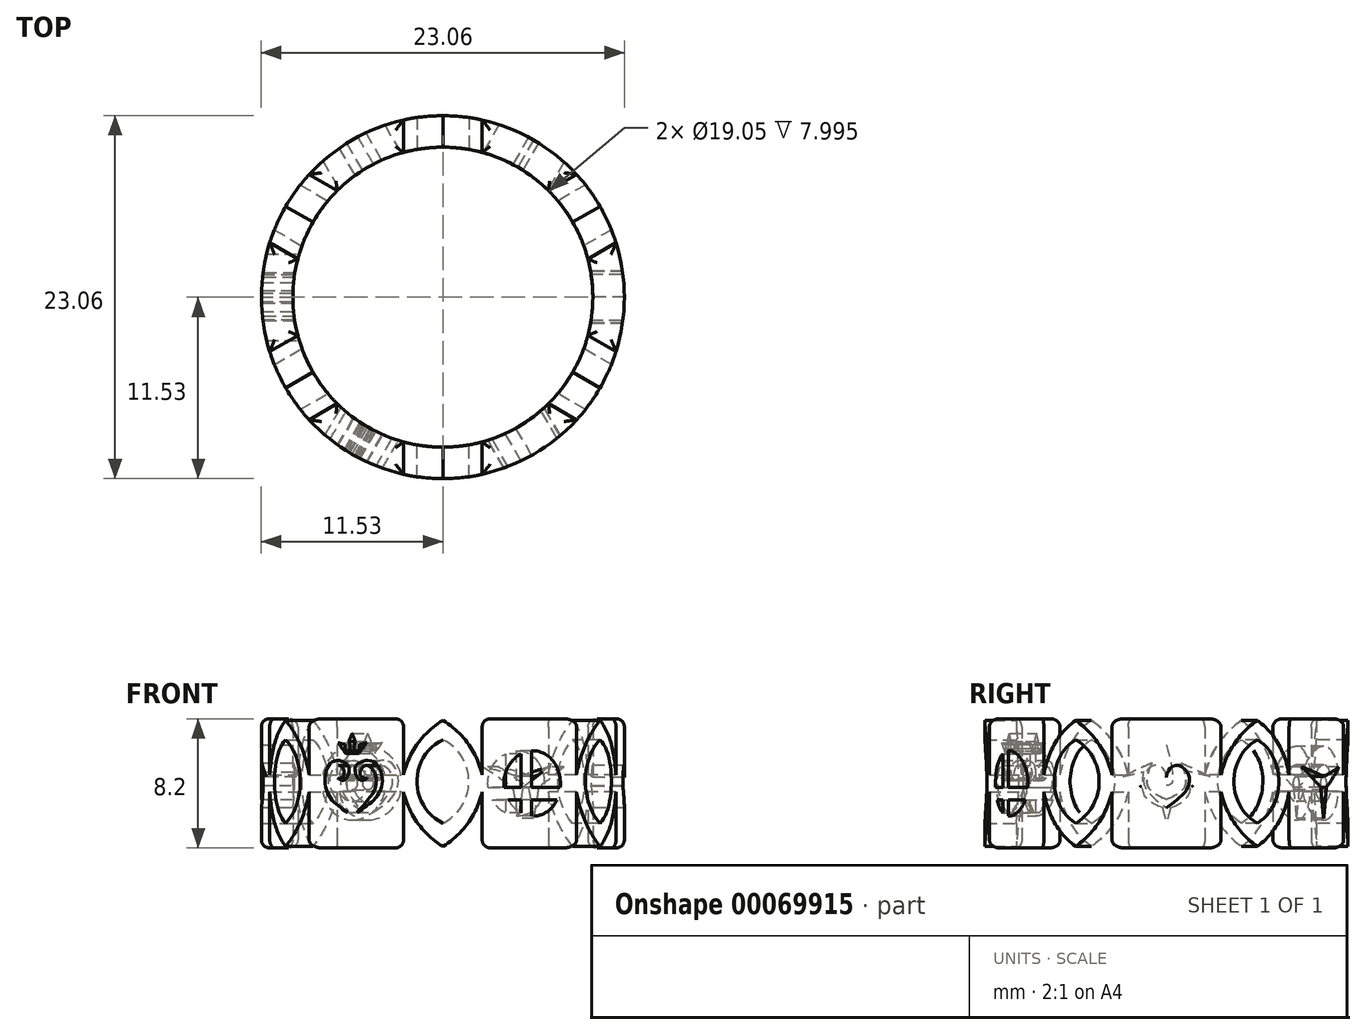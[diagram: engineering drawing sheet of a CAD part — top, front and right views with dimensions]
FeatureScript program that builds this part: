
annotation { "Feature Type Name" : "Feature", "Feature Type Description" : "" }
export const myFeature = defineFeature(function(context is Context, id is Id, definition is map)
    precondition{}
    {
        {
            var Q0;
            Q0=qCreatedBy(makeId("Front.planeOp"),FACE);
            var sketch = newSketch(context, id + "F0", { "sketchPlane" : qUnion([Q0])});
            skLineSegment(sketch, "E0", {"start": v(-9.53, 0) * mm, "end": v(9.53, 0) * mm, "construction": true});
            skLineSegment(sketch, "E1", {"start": v(9.53, -6.35) * mm, "end": v(9.53, 6.35) * mm, "construction": true});
            skLineSegment(sketch, "E2", {"start": v(9.53, -6.35) * mm, "end": v(9.53, 6.35) * mm});
            skLineSegment(sketch, "E3", {"start": v(9.53, -6.35) * mm, "end": v(11.53, -6.35) * mm});
            skLineSegment(sketch, "E4", {"start": v(11.53, 6.35) * mm, "end": v(11.53, -6.35) * mm});
            skLineSegment(sketch, "E5", {"start": v(0, 0) * mm, "end": v(0, 9.27) * mm, "construction": true});
            skLineSegment(sketch, "E6", {"start": v(9.53, 6.35) * mm, "end": v(11.53, 6.35) * mm});
            skSolve(sketch);
        }
        {
            var Q0;
            Q0=makeQuery(id+"F0.imprint","IMPRINT",FACE,{"disambiguationData":[TD([[makeQuery(id+"F0.imprint","IMPRINT",EDGE,{"derivedFrom":sQuery(id+"F0.wireOp",EDGE,"E2")}),-1.0]])]});
            var Q1;
            Q1=sQuery(id+"F0.wireOp",EDGE,"E5");
            revolve(context, id + "F1", {"entities" : qUnion([Q0]), "axis" : qUnion([Q1]), "revolveType" : RevolveType.FULL});
        }
        {
            var Q0;
            Q0=qCreatedBy(makeId("Front.planeOp"),FACE);
            var sketch = newSketch(context, id + "F2", { "sketchPlane" : qUnion([Q0])});
            skArc(sketch, "E7", {"start": v(0, -2.53) * mm, "mid": v(1.65, 0.12) * mm, "end": v(0, 2.77) * mm});
            skArc(sketch, "E8", {"start": v(0, 2.77) * mm, "mid": v(-1.65, 0.12) * mm, "end": v(0, -2.53) * mm});
            skSolve(sketch);
        }
        {
            var Q0;
            Q0=makeQuery(id+"F2.imprint","IMPRINT",FACE,{"disambiguationData":[TD([[makeQuery(id+"F2.imprint","IMPRINT",EDGE,{"derivedFrom":sQuery(id+"F2.wireOp",EDGE,"E7")}),1.0]])]});
            extrude(context, id + "F3", {"entities" : qUnion([Q0]), "operationType" : NewBodyOperationType.REMOVE, "oppositeDirection" : true, "depth" : 25 * mm});
        }
        {
            var Q0;
            Q0=makeQuery(id+"F3.boolean.opBoolean","COPY",FACE,{"derivedFrom":makeQuery(id+"F3.opExtrude","SWEPT_FACE",FACE,{"disambiguationData":[OSD([sQuery(id+"F2.wireOp",EDGE,"E8")])]})});
            var Q1;
            Q1=makeQuery(id+"F3.boolean.opBoolean","COPY",FACE,{"derivedFrom":makeQuery(id+"F3.opExtrude","SWEPT_FACE",FACE,{"disambiguationData":[OSD([sQuery(id+"F2.wireOp",EDGE,"E7")])]})});
            var Q2;
            Q2=makeQuery(id+"F1.opRevolve","SWEPT_FACE",FACE,{"disambiguationData":[OSD([sQuery(id+"F0.wireOp",EDGE,"E2")])]});
            circularPattern(context, id + "F4", {"faces" : qUnion([Q0, Q1]), "axis" : qUnion([Q2]), "angle" : 360 * degree, "instanceCount" : 6, "equalSpace" : true, "patternType" : PatternType.FACE});
        }
        {
            var Q0;
            Q0=qCreatedBy(makeId("Front.planeOp"),FACE);
            var sketch = newSketch(context, id + "F5", { "sketchPlane" : qUnion([Q0])});
            skArc(sketch, "E9", {"start": v(2.5, 0.53) * mm, "mid": v(1.6, 2.52) * mm, "end": v(0, 4) * mm});
            skArc(sketch, "E10.MirrorCS", {"start": v(-2.5, 0.53) * mm, "mid": v(-1.6, 2.52) * mm, "end": v(0, 4) * mm});
            skLineSegment(sketch, "E11", {"start": v(-2.5, 0.53) * mm, "end": v(-2.5, 6.68) * mm});
            skLineSegment(sketch, "E12", {"start": v(-2.5, 6.68) * mm, "end": v(2.5, 6.68) * mm});
            skLineSegment(sketch, "E13", {"start": v(2.5, 6.68) * mm, "end": v(2.5, 0.53) * mm});
            skArc(sketch, "E14.MirrorCS", {"start": v(-2.5, -0.53) * mm, "mid": v(-1.6, -2.52) * mm, "end": v(0, -4) * mm});
            skArc(sketch, "E15.MirrorCS", {"start": v(2.5, -0.53) * mm, "mid": v(1.6, -2.52) * mm, "end": v(0, -4) * mm});
            skLineSegment(sketch, "E16.MirrorCS", {"start": v(2.5, -6.68) * mm, "end": v(2.5, -0.53) * mm});
            skLineSegment(sketch, "E17.MirrorCS", {"start": v(-2.5, -0.53) * mm, "end": v(-2.5, -6.68) * mm});
            skLineSegment(sketch, "E18.MirrorCS", {"start": v(-2.5, -6.68) * mm, "end": v(2.5, -6.68) * mm});
            skSolve(sketch);
        }
        {
            var Q0;
            Q0=makeQuery(id+"F5.imprint","IMPRINT",FACE,{"disambiguationData":[TD([[makeQuery(id+"F5.imprint","IMPRINT",EDGE,{"derivedFrom":sQuery(id+"F5.wireOp",EDGE,"E9")}),-1.0]])]});
            extrude(context, id + "F6", {"entities" : qUnion([Q0]), "operationType" : NewBodyOperationType.REMOVE, "oppositeDirection" : true, "depth" : 25 * mm});
        }
        {
            var Q0;
            Q0=makeQuery(id+"F6.boolean.opBoolean","COPY",FACE,{"derivedFrom":makeQuery(id+"F6.opExtrude","SWEPT_FACE",FACE,{"disambiguationData":[OSD([sQuery(id+"F5.wireOp",EDGE,"E10.MirrorCS")])]})});
            var Q1;
            Q1=makeQuery(id+"F6.boolean.opBoolean","COPY",FACE,{"derivedFrom":makeQuery(id+"F6.opExtrude","SWEPT_FACE",FACE,{"disambiguationData":[OSD([sQuery(id+"F5.wireOp",EDGE,"E9")])]})});
            var Q2;
            Q2=makeQuery(id+"F6.boolean.opBoolean","COPY",FACE,{"derivedFrom":makeQuery(id+"F6.opExtrude","SWEPT_FACE",FACE,{"disambiguationData":[OSD([sQuery(id+"F5.wireOp",EDGE,"E11")])]})});
            var Q3;
            Q3=makeQuery(id+"F6.boolean.opBoolean","COPY",FACE,{"derivedFrom":makeQuery(id+"F6.opExtrude","SWEPT_FACE",FACE,{"disambiguationData":[OSD([sQuery(id+"F5.wireOp",EDGE,"E13")])]})});
            var Q4;
            Q4=makeQuery(id+"F1.opRevolve","SWEPT_FACE",FACE,{"disambiguationData":[OSD([sQuery(id+"F0.wireOp",EDGE,"E4")])]});
            circularPattern(context, id + "F7", {"faces" : qUnion([Q0, Q1, Q2, Q3]), "axis" : qUnion([Q4]), "angle" : 360 * degree, "instanceCount" : 12, "equalSpace" : true, "patternType" : PatternType.FACE});
        }
        {
            var Q0;
            Q0=makeQuery(id+"F1.opRevolve","SWEPT_EDGE",EDGE,{"disambiguationData":[OSD([sQuery(id+"F0.wireOp",EDGE,"E3"),sQuery(id+"F0.wireOp",EDGE,"E4")])]});
            cPlane(context, id + "F8", {"entities" : qUnion([Q0]), "cplaneType" : CPlaneType.LINE_ANGLE, "offset" : 150 * mm, "angle" : 0 * degree, "width" : 150 * mm, "height" : 150 * mm});
        }
        {
            var Q0;
            Q0=makeQuery(id+"F5.imprint","IMPRINT",FACE,{"disambiguationData":[TD([[makeQuery(id+"F5.imprint","IMPRINT",EDGE,{"derivedFrom":sQuery(id+"F5.wireOp",EDGE,"E14.MirrorCS")}),-1.0]])]});
            extrude(context, id + "F9", {"entities" : qUnion([Q0]), "operationType" : NewBodyOperationType.REMOVE, "oppositeDirection" : true, "depth" : 25 * mm});
        }
        {
            var Q0;
            Q0=makeQuery(id+"F9.boolean.opBoolean","COPY",FACE,{"derivedFrom":makeQuery(id+"F9.opExtrude","SWEPT_FACE",FACE,{"disambiguationData":[OSD([sQuery(id+"F5.wireOp",EDGE,"E16.MirrorCS")])]})});
            var Q1;
            Q1=makeQuery(id+"F9.boolean.opBoolean","COPY",FACE,{"derivedFrom":makeQuery(id+"F9.opExtrude","SWEPT_FACE",FACE,{"disambiguationData":[OSD([sQuery(id+"F5.wireOp",EDGE,"E14.MirrorCS")])]})});
            var Q2;
            Q2=makeQuery(id+"F9.boolean.opBoolean","COPY",FACE,{"derivedFrom":makeQuery(id+"F9.opExtrude","SWEPT_FACE",FACE,{"disambiguationData":[OSD([sQuery(id+"F5.wireOp",EDGE,"E15.MirrorCS")])]})});
            var Q3;
            Q3=makeQuery(id+"F9.boolean.opBoolean","COPY",FACE,{"derivedFrom":makeQuery(id+"F9.opExtrude","SWEPT_FACE",FACE,{"disambiguationData":[OSD([sQuery(id+"F5.wireOp",EDGE,"E17.MirrorCS")])]})});
            var Q4;
            Q4=makeQuery(id+"F1.opRevolve","SWEPT_FACE",FACE,{"disambiguationData":[OSD([sQuery(id+"F0.wireOp",EDGE,"E4")])]});
            circularPattern(context, id + "F10", {"faces" : qUnion([Q0, Q1, Q2, Q3]), "axis" : qUnion([Q4]), "angle" : 360 * degree, "instanceCount" : 12, "oppositeDirection" : true, "equalSpace" : true, "patternType" : PatternType.FACE});
        }
        {
            var Q0;
            Q0=qCreatedBy(makeId("Front.planeOp"),FACE);
            var sketch = newSketch(context, id + "F11", { "sketchPlane" : qUnion([Q0])});
            skLineSegment(sketch, "E19.bottom", {"start": v(-11.85, 7.08) * mm, "end": v(-8.83, 7.08) * mm});
            skLineSegment(sketch, "E19.top", {"start": v(-11.85, 4.1) * mm, "end": v(-8.83, 4.1) * mm});
            skLineSegment(sketch, "E19.left", {"start": v(-11.85, 7.08) * mm, "end": v(-11.85, 4.1) * mm});
            skLineSegment(sketch, "E19.right", {"start": v(-8.83, 7.08) * mm, "end": v(-8.83, 4.1) * mm});
            skLineSegment(sketch, "E20.MirrorCS", {"start": v(-11.85, -7.08) * mm, "end": v(-11.85, -4.1) * mm});
            skLineSegment(sketch, "E21.MirrorCS", {"start": v(-11.85, -4.1) * mm, "end": v(-8.83, -4.1) * mm});
            skLineSegment(sketch, "E22.MirrorCS", {"start": v(-8.83, -7.08) * mm, "end": v(-8.83, -4.1) * mm});
            skLineSegment(sketch, "E23.MirrorCS", {"start": v(-11.85, -7.08) * mm, "end": v(-8.83, -7.08) * mm});
            skSolve(sketch);
        }
        {
            var Q0;
            Q0=makeQuery(id+"F11.imprint","IMPRINT",FACE,{"disambiguationData":[TD([[makeQuery(id+"F11.imprint","IMPRINT",EDGE,{"derivedFrom":sQuery(id+"F11.wireOp",EDGE,"E19.bottom")}),-1.0]])]});
            var Q1;
            Q1=sQuery(id+"F0.wireOp",EDGE,"E5");
            revolve(context, id + "F12", {"operationType" : NewBodyOperationType.REMOVE, "entities" : qUnion([Q0]), "axis" : qUnion([Q1]), "revolveType" : RevolveType.FULL, "oppositeDirection" : true});
        }
        {
            var Q0;
            Q0=makeQuery(id+"F11.imprint","IMPRINT",FACE,{"disambiguationData":[TD([[makeQuery(id+"F11.imprint","IMPRINT",EDGE,{"derivedFrom":sQuery(id+"F11.wireOp",EDGE,"E20.MirrorCS")}),-1.0]])]});
            var Q1;
            Q1=sQuery(id+"F0.wireOp",EDGE,"E5");
            revolve(context, id + "F13", {"operationType" : NewBodyOperationType.REMOVE, "entities" : qUnion([Q0]), "axis" : qUnion([Q1]), "revolveType" : RevolveType.FULL, "oppositeDirection" : true});
        }
        {
            var Q0;
            Q0=makeQuery(id+"F13.boolean.opBoolean","INTERSECT",EDGE,{"disambiguationData":[OD(3.0)],"derivedFrom":[makeQuery(id+"F1.opRevolve","SWEPT_FACE",FACE,{"disambiguationData":[OSD([sQuery(id+"F0.wireOp",EDGE,"E2")])]}),makeQuery(id+"F13.opRevolve","SWEPT_FACE",FACE,{"disambiguationData":[OSD([sQuery(id+"F11.wireOp",EDGE,"E21.MirrorCS")])]})]});
            var Q1;
            Q1=makeQuery(id+"F13.boolean.opBoolean","INTERSECT",EDGE,{"disambiguationData":[OD(4.0)],"derivedFrom":[makeQuery(id+"F1.opRevolve","SWEPT_FACE",FACE,{"disambiguationData":[OSD([sQuery(id+"F0.wireOp",EDGE,"E2")])]}),makeQuery(id+"F13.opRevolve","SWEPT_FACE",FACE,{"disambiguationData":[OSD([sQuery(id+"F11.wireOp",EDGE,"E21.MirrorCS")])]})]});
            var Q2;
            Q2=makeQuery(id+"F13.boolean.opBoolean","INTERSECT",EDGE,{"disambiguationData":[OD(5.0)],"derivedFrom":[makeQuery(id+"F1.opRevolve","SWEPT_FACE",FACE,{"disambiguationData":[OSD([sQuery(id+"F0.wireOp",EDGE,"E2")])]}),makeQuery(id+"F13.opRevolve","SWEPT_FACE",FACE,{"disambiguationData":[OSD([sQuery(id+"F11.wireOp",EDGE,"E21.MirrorCS")])]})]});
            var Q3;
            Q3=makeQuery(id+"F13.boolean.opBoolean","INTERSECT",EDGE,{"disambiguationData":[OD(0.0)],"derivedFrom":[makeQuery(id+"F1.opRevolve","SWEPT_FACE",FACE,{"disambiguationData":[OSD([sQuery(id+"F0.wireOp",EDGE,"E2")])]}),makeQuery(id+"F13.opRevolve","SWEPT_FACE",FACE,{"disambiguationData":[OSD([sQuery(id+"F11.wireOp",EDGE,"E21.MirrorCS")])]})]});
            var Q4;
            Q4=makeQuery(id+"F13.boolean.opBoolean","INTERSECT",EDGE,{"disambiguationData":[OD(1.0)],"derivedFrom":[makeQuery(id+"F1.opRevolve","SWEPT_FACE",FACE,{"disambiguationData":[OSD([sQuery(id+"F0.wireOp",EDGE,"E2")])]}),makeQuery(id+"F13.opRevolve","SWEPT_FACE",FACE,{"disambiguationData":[OSD([sQuery(id+"F11.wireOp",EDGE,"E21.MirrorCS")])]})]});
            var Q5;
            Q5=makeQuery(id+"F13.boolean.opBoolean","INTERSECT",EDGE,{"disambiguationData":[OD(2.0)],"derivedFrom":[makeQuery(id+"F1.opRevolve","SWEPT_FACE",FACE,{"disambiguationData":[OSD([sQuery(id+"F0.wireOp",EDGE,"E2")])]}),makeQuery(id+"F13.opRevolve","SWEPT_FACE",FACE,{"disambiguationData":[OSD([sQuery(id+"F11.wireOp",EDGE,"E21.MirrorCS")])]})]});
            var Q6;
            Q6=makeQuery(id+"F12.boolean.opBoolean","INTERSECT",EDGE,{"disambiguationData":[OD(4.0)],"derivedFrom":[makeQuery(id+"F1.opRevolve","SWEPT_FACE",FACE,{"disambiguationData":[OSD([sQuery(id+"F0.wireOp",EDGE,"E2")])]}),makeQuery(id+"F12.opRevolve","SWEPT_FACE",FACE,{"disambiguationData":[OSD([sQuery(id+"F11.wireOp",EDGE,"E19.top")])]})]});
            var Q7;
            Q7=makeQuery(id+"F12.boolean.opBoolean","INTERSECT",EDGE,{"disambiguationData":[OD(3.0)],"derivedFrom":[makeQuery(id+"F1.opRevolve","SWEPT_FACE",FACE,{"disambiguationData":[OSD([sQuery(id+"F0.wireOp",EDGE,"E2")])]}),makeQuery(id+"F12.opRevolve","SWEPT_FACE",FACE,{"disambiguationData":[OSD([sQuery(id+"F11.wireOp",EDGE,"E19.top")])]})]});
            var Q8;
            Q8=makeQuery(id+"F12.boolean.opBoolean","INTERSECT",EDGE,{"disambiguationData":[OD(2.0)],"derivedFrom":[makeQuery(id+"F1.opRevolve","SWEPT_FACE",FACE,{"disambiguationData":[OSD([sQuery(id+"F0.wireOp",EDGE,"E2")])]}),makeQuery(id+"F12.opRevolve","SWEPT_FACE",FACE,{"disambiguationData":[OSD([sQuery(id+"F11.wireOp",EDGE,"E19.top")])]})]});
            var Q9;
            Q9=makeQuery(id+"F12.boolean.opBoolean","INTERSECT",EDGE,{"disambiguationData":[OD(1.0)],"derivedFrom":[makeQuery(id+"F1.opRevolve","SWEPT_FACE",FACE,{"disambiguationData":[OSD([sQuery(id+"F0.wireOp",EDGE,"E2")])]}),makeQuery(id+"F12.opRevolve","SWEPT_FACE",FACE,{"disambiguationData":[OSD([sQuery(id+"F11.wireOp",EDGE,"E19.top")])]})]});
            var Q10;
            Q10=makeQuery(id+"F12.boolean.opBoolean","INTERSECT",EDGE,{"disambiguationData":[OD(0.0)],"derivedFrom":[makeQuery(id+"F1.opRevolve","SWEPT_FACE",FACE,{"disambiguationData":[OSD([sQuery(id+"F0.wireOp",EDGE,"E2")])]}),makeQuery(id+"F12.opRevolve","SWEPT_FACE",FACE,{"disambiguationData":[OSD([sQuery(id+"F11.wireOp",EDGE,"E19.top")])]})]});
            var Q11;
            Q11=makeQuery(id+"F12.boolean.opBoolean","INTERSECT",EDGE,{"disambiguationData":[OD(5.0)],"derivedFrom":[makeQuery(id+"F1.opRevolve","SWEPT_FACE",FACE,{"disambiguationData":[OSD([sQuery(id+"F0.wireOp",EDGE,"E2")])]}),makeQuery(id+"F12.opRevolve","SWEPT_FACE",FACE,{"disambiguationData":[OSD([sQuery(id+"F11.wireOp",EDGE,"E19.top")])]})]});
            fillet(context, id + "F14", {"entities" : qUnion([Q0, Q1, Q2, Q3, Q4, Q5, Q6, Q7, Q8, Q9, Q10, Q11]), "radius" : .5 * mm, "tangentPropagation" : true, "allowEdgeOverflow" : false});
        }
        {
            var Q0;
            Q0=makeQuery(id+"F12.boolean.opBoolean","INTERSECT",EDGE,{"disambiguationData":[OD(2.0)],"derivedFrom":[makeQuery(id+"F1.opRevolve","SWEPT_FACE",FACE,{"disambiguationData":[OSD([sQuery(id+"F0.wireOp",EDGE,"E4")])]}),makeQuery(id+"F12.opRevolve","SWEPT_FACE",FACE,{"disambiguationData":[OSD([sQuery(id+"F11.wireOp",EDGE,"E19.top")])]})]});
            var Q1;
            Q1=makeQuery(id+"F13.boolean.opBoolean","INTERSECT",EDGE,{"disambiguationData":[OD(5.0)],"derivedFrom":[makeQuery(id+"F1.opRevolve","SWEPT_FACE",FACE,{"disambiguationData":[OSD([sQuery(id+"F0.wireOp",EDGE,"E4")])]}),makeQuery(id+"F13.opRevolve","SWEPT_FACE",FACE,{"disambiguationData":[OSD([sQuery(id+"F11.wireOp",EDGE,"E21.MirrorCS")])]})]});
            var Q2;
            Q2=makeQuery(id+"F13.boolean.opBoolean","INTERSECT",EDGE,{"disambiguationData":[OD(4.0)],"derivedFrom":[makeQuery(id+"F1.opRevolve","SWEPT_FACE",FACE,{"disambiguationData":[OSD([sQuery(id+"F0.wireOp",EDGE,"E4")])]}),makeQuery(id+"F13.opRevolve","SWEPT_FACE",FACE,{"disambiguationData":[OSD([sQuery(id+"F11.wireOp",EDGE,"E21.MirrorCS")])]})]});
            var Q3;
            Q3=makeQuery(id+"F12.boolean.opBoolean","INTERSECT",EDGE,{"disambiguationData":[OD(3.0)],"derivedFrom":[makeQuery(id+"F1.opRevolve","SWEPT_FACE",FACE,{"disambiguationData":[OSD([sQuery(id+"F0.wireOp",EDGE,"E4")])]}),makeQuery(id+"F12.opRevolve","SWEPT_FACE",FACE,{"disambiguationData":[OSD([sQuery(id+"F11.wireOp",EDGE,"E19.top")])]})]});
            var Q4;
            Q4=makeQuery(id+"F13.boolean.opBoolean","INTERSECT",EDGE,{"disambiguationData":[OD(3.0)],"derivedFrom":[makeQuery(id+"F1.opRevolve","SWEPT_FACE",FACE,{"disambiguationData":[OSD([sQuery(id+"F0.wireOp",EDGE,"E4")])]}),makeQuery(id+"F13.opRevolve","SWEPT_FACE",FACE,{"disambiguationData":[OSD([sQuery(id+"F11.wireOp",EDGE,"E21.MirrorCS")])]})]});
            var Q5;
            Q5=makeQuery(id+"F12.boolean.opBoolean","INTERSECT",EDGE,{"disambiguationData":[OD(4.0)],"derivedFrom":[makeQuery(id+"F1.opRevolve","SWEPT_FACE",FACE,{"disambiguationData":[OSD([sQuery(id+"F0.wireOp",EDGE,"E4")])]}),makeQuery(id+"F12.opRevolve","SWEPT_FACE",FACE,{"disambiguationData":[OSD([sQuery(id+"F11.wireOp",EDGE,"E19.top")])]})]});
            var Q6;
            Q6=makeQuery(id+"F12.boolean.opBoolean","INTERSECT",EDGE,{"disambiguationData":[OD(5.0)],"derivedFrom":[makeQuery(id+"F1.opRevolve","SWEPT_FACE",FACE,{"disambiguationData":[OSD([sQuery(id+"F0.wireOp",EDGE,"E4")])]}),makeQuery(id+"F12.opRevolve","SWEPT_FACE",FACE,{"disambiguationData":[OSD([sQuery(id+"F11.wireOp",EDGE,"E19.top")])]})]});
            var Q7;
            Q7=makeQuery(id+"F13.boolean.opBoolean","INTERSECT",EDGE,{"disambiguationData":[OD(2.0)],"derivedFrom":[makeQuery(id+"F1.opRevolve","SWEPT_FACE",FACE,{"disambiguationData":[OSD([sQuery(id+"F0.wireOp",EDGE,"E4")])]}),makeQuery(id+"F13.opRevolve","SWEPT_FACE",FACE,{"disambiguationData":[OSD([sQuery(id+"F11.wireOp",EDGE,"E21.MirrorCS")])]})]});
            var Q8;
            Q8=makeQuery(id+"F12.boolean.opBoolean","INTERSECT",EDGE,{"disambiguationData":[OD(0.0)],"derivedFrom":[makeQuery(id+"F1.opRevolve","SWEPT_FACE",FACE,{"disambiguationData":[OSD([sQuery(id+"F0.wireOp",EDGE,"E4")])]}),makeQuery(id+"F12.opRevolve","SWEPT_FACE",FACE,{"disambiguationData":[OSD([sQuery(id+"F11.wireOp",EDGE,"E19.top")])]})]});
            var Q9;
            Q9=makeQuery(id+"F13.boolean.opBoolean","INTERSECT",EDGE,{"disambiguationData":[OD(1.0)],"derivedFrom":[makeQuery(id+"F1.opRevolve","SWEPT_FACE",FACE,{"disambiguationData":[OSD([sQuery(id+"F0.wireOp",EDGE,"E4")])]}),makeQuery(id+"F13.opRevolve","SWEPT_FACE",FACE,{"disambiguationData":[OSD([sQuery(id+"F11.wireOp",EDGE,"E21.MirrorCS")])]})]});
            var Q10;
            Q10=makeQuery(id+"F13.boolean.opBoolean","INTERSECT",EDGE,{"disambiguationData":[OD(0.0)],"derivedFrom":[makeQuery(id+"F1.opRevolve","SWEPT_FACE",FACE,{"disambiguationData":[OSD([sQuery(id+"F0.wireOp",EDGE,"E4")])]}),makeQuery(id+"F13.opRevolve","SWEPT_FACE",FACE,{"disambiguationData":[OSD([sQuery(id+"F11.wireOp",EDGE,"E21.MirrorCS")])]})]});
            var Q11;
            Q11=makeQuery(id+"F12.boolean.opBoolean","INTERSECT",EDGE,{"disambiguationData":[OD(1.0)],"derivedFrom":[makeQuery(id+"F1.opRevolve","SWEPT_FACE",FACE,{"disambiguationData":[OSD([sQuery(id+"F0.wireOp",EDGE,"E4")])]}),makeQuery(id+"F12.opRevolve","SWEPT_FACE",FACE,{"disambiguationData":[OSD([sQuery(id+"F11.wireOp",EDGE,"E19.top")])]})]});
            fillet(context, id + "F15", {"entities" : qUnion([Q0, Q1, Q2, Q3, Q4, Q5, Q6, Q7, Q8, Q9, Q10, Q11]), "radius" : .5 * mm, "tangentPropagation" : true, "allowEdgeOverflow" : false});
        }
        {
            var Q0;
            Q0=makeQuery(id+"F12.boolean.opBoolean","INTERSECT",EDGE,{"derivedFrom":[makeQuery(id+"F7.opPattern","COPY",FACE,{"derivedFrom":makeQuery(id+"F6.boolean.opBoolean","COPY",FACE,{"derivedFrom":makeQuery(id+"F6.opExtrude","SWEPT_FACE",FACE,{"disambiguationData":[OSD([sQuery(id+"F5.wireOp",EDGE,"E11")])]})}),"instanceName":"6"}),makeQuery(id+"F12.opRevolve","SWEPT_FACE",FACE,{"disambiguationData":[OSD([sQuery(id+"F11.wireOp",EDGE,"E19.top")])]})]});
            var Q1;
            Q1=makeQuery(id+"F12.boolean.opBoolean","INTERSECT",EDGE,{"derivedFrom":[makeQuery(id+"F7.opPattern","COPY",FACE,{"derivedFrom":makeQuery(id+"F6.boolean.opBoolean","COPY",FACE,{"derivedFrom":makeQuery(id+"F6.opExtrude","SWEPT_FACE",FACE,{"disambiguationData":[OSD([sQuery(id+"F5.wireOp",EDGE,"E11")])]})}),"instanceName":"4"}),makeQuery(id+"F12.opRevolve","SWEPT_FACE",FACE,{"disambiguationData":[OSD([sQuery(id+"F11.wireOp",EDGE,"E19.top")])]})]});
            var Q2;
            Q2=makeQuery(id+"F12.boolean.opBoolean","INTERSECT",EDGE,{"derivedFrom":[makeQuery(id+"F7.opPattern","COPY",FACE,{"derivedFrom":makeQuery(id+"F6.boolean.opBoolean","COPY",FACE,{"derivedFrom":makeQuery(id+"F6.opExtrude","SWEPT_FACE",FACE,{"disambiguationData":[OSD([sQuery(id+"F5.wireOp",EDGE,"E13")])]})}),"instanceName":"4"}),makeQuery(id+"F12.opRevolve","SWEPT_FACE",FACE,{"disambiguationData":[OSD([sQuery(id+"F11.wireOp",EDGE,"E19.top")])]})]});
            var Q3;
            Q3=makeQuery(id+"F12.boolean.opBoolean","INTERSECT",EDGE,{"derivedFrom":[makeQuery(id+"F7.opPattern","COPY",FACE,{"derivedFrom":makeQuery(id+"F6.boolean.opBoolean","COPY",FACE,{"derivedFrom":makeQuery(id+"F6.opExtrude","SWEPT_FACE",FACE,{"disambiguationData":[OSD([sQuery(id+"F5.wireOp",EDGE,"E13")])]})}),"instanceName":"2"}),makeQuery(id+"F12.opRevolve","SWEPT_FACE",FACE,{"disambiguationData":[OSD([sQuery(id+"F11.wireOp",EDGE,"E19.top")])]})]});
            var Q4;
            Q4=makeQuery(id+"F12.boolean.opBoolean","INTERSECT",EDGE,{"derivedFrom":[makeQuery(id+"F7.opPattern","COPY",FACE,{"derivedFrom":makeQuery(id+"F6.boolean.opBoolean","COPY",FACE,{"derivedFrom":makeQuery(id+"F6.opExtrude","SWEPT_FACE",FACE,{"disambiguationData":[OSD([sQuery(id+"F5.wireOp",EDGE,"E11")])]})}),"instanceName":"2"}),makeQuery(id+"F12.opRevolve","SWEPT_FACE",FACE,{"disambiguationData":[OSD([sQuery(id+"F11.wireOp",EDGE,"E19.top")])]})]});
            var Q5;
            Q5=makeQuery(id+"F12.boolean.opBoolean","INTERSECT",EDGE,{"derivedFrom":[makeQuery(id+"F6.boolean.opBoolean","COPY",FACE,{"derivedFrom":makeQuery(id+"F6.opExtrude","SWEPT_FACE",FACE,{"disambiguationData":[OSD([sQuery(id+"F5.wireOp",EDGE,"E13")])]})}),makeQuery(id+"F12.opRevolve","SWEPT_FACE",FACE,{"disambiguationData":[OSD([sQuery(id+"F11.wireOp",EDGE,"E19.top")])]})]});
            var Q6;
            Q6=makeQuery(id+"F12.boolean.opBoolean","INTERSECT",EDGE,{"derivedFrom":[makeQuery(id+"F6.boolean.opBoolean","COPY",FACE,{"derivedFrom":makeQuery(id+"F6.opExtrude","SWEPT_FACE",FACE,{"disambiguationData":[OSD([sQuery(id+"F5.wireOp",EDGE,"E11")])]})}),makeQuery(id+"F12.opRevolve","SWEPT_FACE",FACE,{"disambiguationData":[OSD([sQuery(id+"F11.wireOp",EDGE,"E19.top")])]})]});
            var Q7;
            Q7=makeQuery(id+"F12.boolean.opBoolean","INTERSECT",EDGE,{"derivedFrom":[makeQuery(id+"F7.opPattern","COPY",FACE,{"derivedFrom":makeQuery(id+"F6.boolean.opBoolean","COPY",FACE,{"derivedFrom":makeQuery(id+"F6.opExtrude","SWEPT_FACE",FACE,{"disambiguationData":[OSD([sQuery(id+"F5.wireOp",EDGE,"E13")])]})}),"instanceName":"10"}),makeQuery(id+"F12.opRevolve","SWEPT_FACE",FACE,{"disambiguationData":[OSD([sQuery(id+"F11.wireOp",EDGE,"E19.top")])]})]});
            var Q8;
            Q8=makeQuery(id+"F12.boolean.opBoolean","INTERSECT",EDGE,{"derivedFrom":[makeQuery(id+"F7.opPattern","COPY",FACE,{"derivedFrom":makeQuery(id+"F6.boolean.opBoolean","COPY",FACE,{"derivedFrom":makeQuery(id+"F6.opExtrude","SWEPT_FACE",FACE,{"disambiguationData":[OSD([sQuery(id+"F5.wireOp",EDGE,"E11")])]})}),"instanceName":"10"}),makeQuery(id+"F12.opRevolve","SWEPT_FACE",FACE,{"disambiguationData":[OSD([sQuery(id+"F11.wireOp",EDGE,"E19.top")])]})]});
            var Q9;
            Q9=makeQuery(id+"F12.boolean.opBoolean","INTERSECT",EDGE,{"derivedFrom":[makeQuery(id+"F7.opPattern","COPY",FACE,{"derivedFrom":makeQuery(id+"F6.boolean.opBoolean","COPY",FACE,{"derivedFrom":makeQuery(id+"F6.opExtrude","SWEPT_FACE",FACE,{"disambiguationData":[OSD([sQuery(id+"F5.wireOp",EDGE,"E13")])]})}),"instanceName":"8"}),makeQuery(id+"F12.opRevolve","SWEPT_FACE",FACE,{"disambiguationData":[OSD([sQuery(id+"F11.wireOp",EDGE,"E19.top")])]})]});
            var Q10;
            Q10=makeQuery(id+"F12.boolean.opBoolean","INTERSECT",EDGE,{"derivedFrom":[makeQuery(id+"F7.opPattern","COPY",FACE,{"derivedFrom":makeQuery(id+"F6.boolean.opBoolean","COPY",FACE,{"derivedFrom":makeQuery(id+"F6.opExtrude","SWEPT_FACE",FACE,{"disambiguationData":[OSD([sQuery(id+"F5.wireOp",EDGE,"E11")])]})}),"instanceName":"8"}),makeQuery(id+"F12.opRevolve","SWEPT_FACE",FACE,{"disambiguationData":[OSD([sQuery(id+"F11.wireOp",EDGE,"E19.top")])]})]});
            var Q11;
            Q11=makeQuery(id+"F12.boolean.opBoolean","INTERSECT",EDGE,{"derivedFrom":[makeQuery(id+"F7.opPattern","COPY",FACE,{"derivedFrom":makeQuery(id+"F6.boolean.opBoolean","COPY",FACE,{"derivedFrom":makeQuery(id+"F6.opExtrude","SWEPT_FACE",FACE,{"disambiguationData":[OSD([sQuery(id+"F5.wireOp",EDGE,"E13")])]})}),"instanceName":"6"}),makeQuery(id+"F12.opRevolve","SWEPT_FACE",FACE,{"disambiguationData":[OSD([sQuery(id+"F11.wireOp",EDGE,"E19.top")])]})]});
            var Q12;
            Q12=makeQuery(id+"F13.boolean.opBoolean","INTERSECT",EDGE,{"derivedFrom":[makeQuery(id+"F10.opPattern","COPY",FACE,{"derivedFrom":makeQuery(id+"F9.boolean.opBoolean","COPY",FACE,{"derivedFrom":makeQuery(id+"F9.opExtrude","SWEPT_FACE",FACE,{"disambiguationData":[OSD([sQuery(id+"F5.wireOp",EDGE,"E17.MirrorCS")])]})}),"instanceName":"4"}),makeQuery(id+"F13.opRevolve","SWEPT_FACE",FACE,{"disambiguationData":[OSD([sQuery(id+"F11.wireOp",EDGE,"E21.MirrorCS")])]})]});
            var Q13;
            Q13=makeQuery(id+"F13.boolean.opBoolean","INTERSECT",EDGE,{"derivedFrom":[makeQuery(id+"F10.opPattern","COPY",FACE,{"derivedFrom":makeQuery(id+"F9.boolean.opBoolean","COPY",FACE,{"derivedFrom":makeQuery(id+"F9.opExtrude","SWEPT_FACE",FACE,{"disambiguationData":[OSD([sQuery(id+"F5.wireOp",EDGE,"E16.MirrorCS")])]})}),"instanceName":"4"}),makeQuery(id+"F13.opRevolve","SWEPT_FACE",FACE,{"disambiguationData":[OSD([sQuery(id+"F11.wireOp",EDGE,"E21.MirrorCS")])]})]});
            var Q14;
            Q14=makeQuery(id+"F13.boolean.opBoolean","INTERSECT",EDGE,{"derivedFrom":[makeQuery(id+"F10.opPattern","COPY",FACE,{"derivedFrom":makeQuery(id+"F9.boolean.opBoolean","COPY",FACE,{"derivedFrom":makeQuery(id+"F9.opExtrude","SWEPT_FACE",FACE,{"disambiguationData":[OSD([sQuery(id+"F5.wireOp",EDGE,"E16.MirrorCS")])]})}),"instanceName":"6"}),makeQuery(id+"F13.opRevolve","SWEPT_FACE",FACE,{"disambiguationData":[OSD([sQuery(id+"F11.wireOp",EDGE,"E21.MirrorCS")])]})]});
            var Q15;
            Q15=makeQuery(id+"F13.boolean.opBoolean","INTERSECT",EDGE,{"derivedFrom":[makeQuery(id+"F10.opPattern","COPY",FACE,{"derivedFrom":makeQuery(id+"F9.boolean.opBoolean","COPY",FACE,{"derivedFrom":makeQuery(id+"F9.opExtrude","SWEPT_FACE",FACE,{"disambiguationData":[OSD([sQuery(id+"F5.wireOp",EDGE,"E17.MirrorCS")])]})}),"instanceName":"6"}),makeQuery(id+"F13.opRevolve","SWEPT_FACE",FACE,{"disambiguationData":[OSD([sQuery(id+"F11.wireOp",EDGE,"E21.MirrorCS")])]})]});
            var Q16;
            Q16=makeQuery(id+"F13.boolean.opBoolean","INTERSECT",EDGE,{"derivedFrom":[makeQuery(id+"F10.opPattern","COPY",FACE,{"derivedFrom":makeQuery(id+"F9.boolean.opBoolean","COPY",FACE,{"derivedFrom":makeQuery(id+"F9.opExtrude","SWEPT_FACE",FACE,{"disambiguationData":[OSD([sQuery(id+"F5.wireOp",EDGE,"E16.MirrorCS")])]})}),"instanceName":"8"}),makeQuery(id+"F13.opRevolve","SWEPT_FACE",FACE,{"disambiguationData":[OSD([sQuery(id+"F11.wireOp",EDGE,"E21.MirrorCS")])]})]});
            var Q17;
            Q17=makeQuery(id+"F13.boolean.opBoolean","INTERSECT",EDGE,{"derivedFrom":[makeQuery(id+"F10.opPattern","COPY",FACE,{"derivedFrom":makeQuery(id+"F9.boolean.opBoolean","COPY",FACE,{"derivedFrom":makeQuery(id+"F9.opExtrude","SWEPT_FACE",FACE,{"disambiguationData":[OSD([sQuery(id+"F5.wireOp",EDGE,"E17.MirrorCS")])]})}),"instanceName":"8"}),makeQuery(id+"F13.opRevolve","SWEPT_FACE",FACE,{"disambiguationData":[OSD([sQuery(id+"F11.wireOp",EDGE,"E21.MirrorCS")])]})]});
            var Q18;
            Q18=makeQuery(id+"F13.boolean.opBoolean","INTERSECT",EDGE,{"derivedFrom":[makeQuery(id+"F10.opPattern","COPY",FACE,{"derivedFrom":makeQuery(id+"F9.boolean.opBoolean","COPY",FACE,{"derivedFrom":makeQuery(id+"F9.opExtrude","SWEPT_FACE",FACE,{"disambiguationData":[OSD([sQuery(id+"F5.wireOp",EDGE,"E16.MirrorCS")])]})}),"instanceName":"10"}),makeQuery(id+"F13.opRevolve","SWEPT_FACE",FACE,{"disambiguationData":[OSD([sQuery(id+"F11.wireOp",EDGE,"E21.MirrorCS")])]})]});
            var Q19;
            Q19=makeQuery(id+"F13.boolean.opBoolean","INTERSECT",EDGE,{"derivedFrom":[makeQuery(id+"F10.opPattern","COPY",FACE,{"derivedFrom":makeQuery(id+"F9.boolean.opBoolean","COPY",FACE,{"derivedFrom":makeQuery(id+"F9.opExtrude","SWEPT_FACE",FACE,{"disambiguationData":[OSD([sQuery(id+"F5.wireOp",EDGE,"E17.MirrorCS")])]})}),"instanceName":"10"}),makeQuery(id+"F13.opRevolve","SWEPT_FACE",FACE,{"disambiguationData":[OSD([sQuery(id+"F11.wireOp",EDGE,"E21.MirrorCS")])]})]});
            var Q20;
            Q20=makeQuery(id+"F13.boolean.opBoolean","INTERSECT",EDGE,{"derivedFrom":[makeQuery(id+"F9.boolean.opBoolean","COPY",FACE,{"derivedFrom":makeQuery(id+"F9.opExtrude","SWEPT_FACE",FACE,{"disambiguationData":[OSD([sQuery(id+"F5.wireOp",EDGE,"E16.MirrorCS")])]})}),makeQuery(id+"F13.opRevolve","SWEPT_FACE",FACE,{"disambiguationData":[OSD([sQuery(id+"F11.wireOp",EDGE,"E21.MirrorCS")])]})]});
            var Q21;
            Q21=makeQuery(id+"F13.boolean.opBoolean","INTERSECT",EDGE,{"derivedFrom":[makeQuery(id+"F9.boolean.opBoolean","COPY",FACE,{"derivedFrom":makeQuery(id+"F9.opExtrude","SWEPT_FACE",FACE,{"disambiguationData":[OSD([sQuery(id+"F5.wireOp",EDGE,"E17.MirrorCS")])]})}),makeQuery(id+"F13.opRevolve","SWEPT_FACE",FACE,{"disambiguationData":[OSD([sQuery(id+"F11.wireOp",EDGE,"E21.MirrorCS")])]})]});
            var Q22;
            Q22=makeQuery(id+"F13.boolean.opBoolean","INTERSECT",EDGE,{"derivedFrom":[makeQuery(id+"F10.opPattern","COPY",FACE,{"derivedFrom":makeQuery(id+"F9.boolean.opBoolean","COPY",FACE,{"derivedFrom":makeQuery(id+"F9.opExtrude","SWEPT_FACE",FACE,{"disambiguationData":[OSD([sQuery(id+"F5.wireOp",EDGE,"E16.MirrorCS")])]})}),"instanceName":"2"}),makeQuery(id+"F13.opRevolve","SWEPT_FACE",FACE,{"disambiguationData":[OSD([sQuery(id+"F11.wireOp",EDGE,"E21.MirrorCS")])]})]});
            var Q23;
            Q23=makeQuery(id+"F13.boolean.opBoolean","INTERSECT",EDGE,{"derivedFrom":[makeQuery(id+"F10.opPattern","COPY",FACE,{"derivedFrom":makeQuery(id+"F9.boolean.opBoolean","COPY",FACE,{"derivedFrom":makeQuery(id+"F9.opExtrude","SWEPT_FACE",FACE,{"disambiguationData":[OSD([sQuery(id+"F5.wireOp",EDGE,"E17.MirrorCS")])]})}),"instanceName":"2"}),makeQuery(id+"F13.opRevolve","SWEPT_FACE",FACE,{"disambiguationData":[OSD([sQuery(id+"F11.wireOp",EDGE,"E21.MirrorCS")])]})]});
            fillet(context, id + "F16", {"entities" : qUnion([Q0, Q1, Q2, Q3, Q4, Q5, Q6, Q7, Q8, Q9, Q10, Q11, Q12, Q13, Q14, Q15, Q16, Q17, Q18, Q19, Q20, Q21, Q22, Q23]), "radius" : .5 * mm, "tangentPropagation" : true, "allowEdgeOverflow" : false});
        }
        {
            var Q0;
            Q0=qCreatedBy(makeId("Right.planeOp"),FACE);
            var sketch = newSketch(context, id + "F17", { "sketchPlane" : qUnion([Q0])});
            skFitSpline(sketch, "E24", {"points": [v(0, -1.02) * mm, v(-1.23, 0) * mm, v(-0.92, 1.31) * mm], "startDerivative": vector(-4.87, 1.92) * mm, "endDerivative": vector(1.37, 2.92) * mm});
            skFitSpline(sketch, "E25", {"points": [v(-0.92, 1.31) * mm, v(-2.75, 0.44) * mm], "startDerivative": vector(-1.83, -0.87) * mm, "endDerivative": vector(-1.83, -0.87) * mm});
            skFitSpline(sketch, "E26", {"points": [v(-2.75, 0.44) * mm, v(-1.43, 0.74) * mm], "startDerivative": vector(1.32, 0.3) * mm, "endDerivative": vector(1.32, 0.3) * mm});
            skFitSpline(sketch, "E27", {"points": [v(-1.43, 0.74) * mm, v(-1.13, -1.08) * mm, v(0, -1.58) * mm], "startDerivative": vector(-1.08, -6.2) * mm, "endDerivative": vector(2.82, -0.33) * mm});
            skLineSegment(sketch, "E28", {"start": v(-0.26, -1.53) * mm, "end": v(0, -2.54) * mm});
            skFitSpline(sketch, "E29.MirrorCS", {"points": [v(0, -1.02) * mm, v(1.23, 0) * mm, v(0.92, 1.31) * mm], "startDerivative": vector(4.87, 1.92) * mm, "endDerivative": vector(-1.37, 2.92) * mm});
            skLineSegment(sketch, "E30.MirrorCS", {"start": v(0.26, -1.53) * mm, "end": v(0, -2.54) * mm});
            skFitSpline(sketch, "E31.MirrorCS", {"points": [v(1.43, 0.74) * mm, v(1.13, -1.08) * mm, v(0, -1.58) * mm], "startDerivative": vector(1.08, -6.2) * mm, "endDerivative": vector(-2.82, -0.33) * mm});
            skFitSpline(sketch, "E32.MirrorCS", {"points": [v(2.75, 0.44) * mm, v(1.43, 0.74) * mm], "startDerivative": vector(-1.32, 0.3) * mm, "endDerivative": vector(-1.32, 0.3) * mm});
            skFitSpline(sketch, "E33.MirrorCS", {"points": [v(0.92, 1.31) * mm, v(2.75, 0.44) * mm], "startDerivative": vector(1.83, -0.87) * mm, "endDerivative": vector(1.83, -0.87) * mm});
            skFitSpline(sketch, "E34", {"points": [v(-0.11, 2.06) * mm, v(-0.96, 0.22) * mm, v(0, -0.65) * mm], "startDerivative": vector(-2.53, -3.7) * mm, "endDerivative": vector(2.97, -1.64) * mm});
            skFitSpline(sketch, "E35", {"points": [v(-0.11, 2.06) * mm, v(-0.49, 0.3) * mm, v(0, -0.65) * mm], "startDerivative": vector(-1.8, -3.45) * mm, "endDerivative": vector(2.19, -1.9) * mm});
            skFitSpline(sketch, "E36.MirrorCS", {"points": [v(0.11, 2.06) * mm, v(0.49, 0.3) * mm, v(0, -0.65) * mm], "startDerivative": vector(1.8, -3.45) * mm, "endDerivative": vector(-2.19, -1.9) * mm});
            skFitSpline(sketch, "E37.MirrorCS", {"points": [v(0.11, 2.06) * mm, v(0.96, 0.22) * mm, v(0, -0.65) * mm], "startDerivative": vector(2.53, -3.7) * mm, "endDerivative": vector(-2.97, -1.64) * mm});
            skSolve(sketch);
        }
        {
            var Q0;
            Q0=makeQuery(id+"F17.imprint","IMPRINT",FACE,{"disambiguationData":[TD([[makeQuery(id+"F17.imprint","IMPRINT",EDGE,{"derivedFrom":sQuery(id+"F17.wireOp",EDGE,"E24")}),1.0]])]});
            var Q1;
            {var subQ3=sQuery(id+"F17.wireOp",EDGE,"E28");Q1=makeQuery(id+"F17.imprint","IMPRINT",FACE,{"disambiguationData":[TD([[makeQuery(id+"F17.imprint","IMPRINT",EDGE,{"derivedFrom":subQ3}),1.0]])]});}
            extrude(context, id + "F18", {"entities" : qUnion([Q0, Q1]), "operationType" : NewBodyOperationType.REMOVE, "oppositeDirection" : true, "depth" : 25 * mm});
        }
        {
            var Q0;
            Q0=qCreatedBy(makeId("Right.planeOp"),FACE);
            var sketch = newSketch(context, id + "F19", { "sketchPlane" : qUnion([Q0])});
            skFitSpline(sketch, "E38", {"points": [v(0, 2.43) * mm, v(0.33, 0) * mm, v(0, -0.14) * mm], "startDerivative": vector(1.23, -4.42) * mm, "endDerivative": vector(-1.6, -0.45) * mm});
            skFitSpline(sketch, "E39.MirrorCS", {"points": [v(0, 2.43) * mm, v(-0.33, 0) * mm, v(0, -0.14) * mm], "startDerivative": vector(-1.23, -4.42) * mm, "endDerivative": vector(1.6, -0.45) * mm});
            skSolve(sketch);
        }
        {
            var Q0;
            Q0 = qSketchRegion(id + "F19", true);
            extrude(context, id + "F20", {"entities" : qUnion([Q0]), "operationType" : NewBodyOperationType.REMOVE, "oppositeDirection" : true, "depth" : 25 * mm});
        }
        {
            var Q0;
            Q0=qCreatedBy(id+"F8.planeOp",FACE);
            var Q1;
            Q1=makeQuery(id+"F7.opPattern","COPY",EDGE,{"derivedFrom":makeQuery(id+"F6.boolean.opBoolean","INTERSECT",EDGE,{"derivedFrom":[makeQuery(id+"F1.opRevolve","SWEPT_FACE",FACE,{"disambiguationData":[OSD([sQuery(id+"F0.wireOp",EDGE,"E4")])]}),makeQuery(id+"F6.opExtrude","SWEPT_FACE",FACE,{"disambiguationData":[OSD([sQuery(id+"F5.wireOp",EDGE,"E13")])]})]}),"instanceName":"6"});
            cPlane(context, id + "F21", {"entities" : qUnion([Q0, Q1]), "cplaneType" : CPlaneType.LINE_ANGLE, "offset" : 150 * mm, "angle" : 60 * degree, "width" : 150 * mm, "height" : 150 * mm});
        }
        {
            var Q0;
            Q0=qCreatedBy(makeId("Right.planeOp"),FACE);
            var Q1;
            Q1=makeQuery(id+"F7.opPattern","COPY",EDGE,{"derivedFrom":makeQuery(id+"F6.boolean.opBoolean","INTERSECT",EDGE,{"derivedFrom":[makeQuery(id+"F1.opRevolve","SWEPT_FACE",FACE,{"disambiguationData":[OSD([sQuery(id+"F0.wireOp",EDGE,"E4")])]}),makeQuery(id+"F6.opExtrude","SWEPT_FACE",FACE,{"disambiguationData":[OSD([sQuery(id+"F5.wireOp",EDGE,"E11")])]})]}),"instanceName":"4"});
            cPlane(context, id + "F22", {"entities" : qUnion([Q0, Q1]), "cplaneType" : CPlaneType.LINE_ANGLE, "offset" : 150 * mm, "angle" : 120 * degree, "width" : 150 * mm, "height" : 150 * mm});
        }
        {
            var Q0;
            Q0=qCreatedBy(makeId("Right.planeOp"),FACE);
            var Q1;
            Q1=makeQuery(id+"F7.opPattern","COPY",EDGE,{"derivedFrom":makeQuery(id+"F6.boolean.opBoolean","INTERSECT",EDGE,{"derivedFrom":[makeQuery(id+"F1.opRevolve","SWEPT_FACE",FACE,{"disambiguationData":[OSD([sQuery(id+"F0.wireOp",EDGE,"E4")])]}),makeQuery(id+"F6.opExtrude","SWEPT_FACE",FACE,{"disambiguationData":[OSD([sQuery(id+"F5.wireOp",EDGE,"E11")])]})]}),"instanceName":"2"});
            cPlane(context, id + "F23", {"entities" : qUnion([Q0, Q1]), "cplaneType" : CPlaneType.LINE_ANGLE, "offset" : 150 * mm, "angle" : 300 * degree, "width" : 150 * mm, "height" : 150 * mm});
        }
        {
            var Q0;
            Q0=qCreatedBy(makeId("Front.planeOp"),FACE);
            var Q1;
            Q1=makeQuery(id+"F6.boolean.opBoolean","INTERSECT",EDGE,{"derivedFrom":[makeQuery(id+"F1.opRevolve","SWEPT_FACE",FACE,{"disambiguationData":[OSD([sQuery(id+"F0.wireOp",EDGE,"E4")])]}),makeQuery(id+"F6.opExtrude","SWEPT_FACE",FACE,{"disambiguationData":[OSD([sQuery(id+"F5.wireOp",EDGE,"E11")])]})]});
            cPlane(context, id + "F24", {"entities" : qUnion([Q0, Q1]), "cplaneType" : CPlaneType.LINE_ANGLE, "offset" : 150 * mm, "angle" : 150 * degree, "width" : 150 * mm, "height" : 150 * mm});
        }
        {
            var Q0;
            Q0=makeQuery(id+"F1.opRevolve","SWEPT_BODY",BODY,{"disambiguationData":[OSD([sQuery(id+"F0.wireOp",EDGE,"E2"),sQuery(id+"F0.wireOp",EDGE,"E3"),sQuery(id+"F0.wireOp",EDGE,"E4"),sQuery(id+"F0.wireOp",EDGE,"E6")])]});
            transform(context, id + "F25", {"entities" : qUnion([Q0]), "transformType" : TransformType.TRANSLATION_3D, "dx" : 0 * mm, "dy" : 0 * mm, "dz" : 0 * mm, "makeCopy" : true});
        }
        {
            var Q0;
            Q0=qCreatedBy(id+"F21.planeOp",FACE);
            var sketch = newSketch(context, id + "F26", { "sketchPlane" : qUnion([Q0])});
            skCircle(sketch, "E40", {"center": v(0, 0) * mm, "radius": 2.07 * mm, "construction": true});
            skArc(sketch, "E41", {"start": v(-0.9, 1.87) * mm, "mid": v(-1.82, 1) * mm, "end": v(-2.06, -0.26) * mm});
            skArc(sketch, "E42", {"start": v(-1.8, -1.05) * mm, "mid": v(-1.4, -1.53) * mm, "end": v(-0.9, -1.87) * mm});
            skLineSegment(sketch, "E43", {"start": v(-2.06, -0.26) * mm, "end": v(-0.9, -0.26) * mm});
            skLineSegment(sketch, "E44", {"start": v(-0.9, -0.26) * mm, "end": v(-0.9, 1.87) * mm});
            skLineSegment(sketch, "E45", {"start": v(-1.8, -1.05) * mm, "end": v(-0.9, -1.05) * mm});
            skLineSegment(sketch, "E46", {"start": v(-0.9, -1.05) * mm, "end": v(-0.9, -1.87) * mm});
            skArc(sketch, "E47", {"start": v(2.06, -0.26) * mm, "mid": v(1.5, 1.4) * mm, "end": v(-0.14, 2.07) * mm});
            skArc(sketch, "E48", {"start": v(-0.14, -2.07) * mm, "mid": v(0.97, -1.84) * mm, "end": v(1.8, -1.05) * mm});
            skLineSegment(sketch, "E49", {"start": v(-0.14, 2.07) * mm, "end": v(-0.14, -0.26) * mm});
            skLineSegment(sketch, "E50", {"start": v(-0.14, -0.26) * mm, "end": v(2.06, -0.26) * mm});
            skLineSegment(sketch, "E51", {"start": v(1.8, -1.05) * mm, "end": v(-0.14, -1.05) * mm});
            skLineSegment(sketch, "E52", {"start": v(-0.14, -1.05) * mm, "end": v(-0.14, -2.07) * mm});
            skSolve(sketch);
        }
        {
            var Q0;
            Q0=makeQuery(id+"F26.imprint","IMPRINT",FACE,{"disambiguationData":[TD([[makeQuery(id+"F26.imprint","IMPRINT",EDGE,{"derivedFrom":sQuery(id+"F26.wireOp",EDGE,"E41")}),1.0]])]});
            var Q1;
            Q1=makeQuery(id+"F26.imprint","IMPRINT",FACE,{"disambiguationData":[TD([[makeQuery(id+"F26.imprint","IMPRINT",EDGE,{"derivedFrom":sQuery(id+"F26.wireOp",EDGE,"E47")}),1.0]])]});
            var Q2;
            Q2=makeQuery(id+"F26.imprint","IMPRINT",FACE,{"disambiguationData":[TD([[makeQuery(id+"F26.imprint","IMPRINT",EDGE,{"derivedFrom":sQuery(id+"F26.wireOp",EDGE,"E48")}),1.0]])]});
            var Q3;
            Q3=makeQuery(id+"F26.imprint","IMPRINT",FACE,{"disambiguationData":[TD([[makeQuery(id+"F26.imprint","IMPRINT",EDGE,{"derivedFrom":sQuery(id+"F26.wireOp",EDGE,"E42")}),1.0]])]});
            var Q4;
            Q4=sQuery(id+"F26.wireOp",EDGE,"E51");
            var Q5;
            Q5=sQuery(id+"F26.wireOp",EDGE,"E50");
            extrude(context, id + "F27", {"entities" : qUnion([Q0, Q1, Q2, Q3]), "operationType" : NewBodyOperationType.REMOVE, "surfaceEntities" : qUnion([Q4, Q5]), "depth" : 25 * mm});
        }
        {
            var Q0;
            Q0=qCreatedBy(makeId("Right.planeOp"),FACE);
            var sketch = newSketch(context, id + "F28", { "sketchPlane" : qUnion([Q0])});
            skFitSpline(sketch, "E53", {"points": [v(2.06, 0.62) * mm, v(1.26, 0.27) * mm, v(0.57, 0.8) * mm, v(0.86, 1.25) * mm, v(3.64, 1.13) * mm, v(4.06, -0.3) * mm, v(0.7, -1.84) * mm], "startDerivative": vector(-1.02, -6.36) * mm, "endDerivative": vector(-16.5, -5.13) * mm});
            skFitSpline(sketch, "E54", {"points": [v(0.7, -1.84) * mm, v(2.21, -1.06) * mm, v(3.38, 0) * mm, v(2.8, 0.97) * mm, v(1.54, 0.8) * mm, v(2.06, 0.62) * mm], "startDerivative": vector(7.93, 3.41) * mm, "endDerivative": vector(17.84, 7.6) * mm});
            skLineSegment(sketch, "E55", {"start": v(0, 0) * mm, "end": v(0, 1.68) * mm, "construction": true});
            skFitSpline(sketch, "E56.MirrorCS", {"points": [v(-0.7, -1.84) * mm, v(-2.21, -1.06) * mm, v(-3.38, 0) * mm, v(-2.8, 0.97) * mm, v(-1.54, 0.8) * mm, v(-2.06, 0.62) * mm], "startDerivative": vector(-7.93, 3.41) * mm, "endDerivative": vector(-17.84, 7.6) * mm});
            skFitSpline(sketch, "E57.MirrorCS", {"points": [v(-2.06, 0.62) * mm, v(-1.26, 0.27) * mm, v(-0.57, 0.8) * mm, v(-0.86, 1.25) * mm, v(-3.64, 1.13) * mm, v(-4.06, -0.3) * mm, v(-0.7, -1.84) * mm], "startDerivative": vector(1.02, -6.36) * mm, "endDerivative": vector(16.5, -5.13) * mm});
            skLineSegment(sketch, "E58", {"start": v(0, 1.9) * mm, "end": v(0.98, 1.9) * mm});
            skLineSegment(sketch, "E59", {"start": v(0.98, 1.9) * mm, "end": v(2.1, 2.58) * mm});
            skLineSegment(sketch, "E60", {"start": v(2.1, 2.58) * mm, "end": v(0.97, 2.46) * mm});
            skLineSegment(sketch, "E61", {"start": v(0.97, 2.46) * mm, "end": v(1, 2.23) * mm});
            skLineSegment(sketch, "E62", {"start": v(1, 2.23) * mm, "end": v(0.33, 2.16) * mm});
            skLineSegment(sketch, "E63", {"start": v(0.33, 2.16) * mm, "end": v(0.7, 2.7) * mm});
            skLineSegment(sketch, "E64", {"start": v(0.7, 2.7) * mm, "end": v(0, 3.17) * mm});
            skLineSegment(sketch, "E65.MirrorCS", {"start": v(0, 1.9) * mm, "end": v(-0.98, 1.9) * mm});
            skLineSegment(sketch, "E66.MirrorCS", {"start": v(-0.98, 1.9) * mm, "end": v(-2.1, 2.58) * mm});
            skLineSegment(sketch, "E67.MirrorCS", {"start": v(-2.1, 2.58) * mm, "end": v(-0.97, 2.46) * mm});
            skLineSegment(sketch, "E68.MirrorCS", {"start": v(-0.97, 2.46) * mm, "end": v(-1, 2.23) * mm});
            skLineSegment(sketch, "E69.MirrorCS", {"start": v(-1, 2.23) * mm, "end": v(-0.33, 2.16) * mm});
            skLineSegment(sketch, "E70.MirrorCS", {"start": v(-0.33, 2.16) * mm, "end": v(-0.7, 2.7) * mm});
            skLineSegment(sketch, "E71.MirrorCS", {"start": v(-0.7, 2.7) * mm, "end": v(0, 3.17) * mm});
            skSolve(sketch);
        }
        {
            var Q0;
            Q0=qCreatedBy(id+"F22.planeOp",FACE);
            var sketch = newSketch(context, id + "F29", { "sketchPlane" : qUnion([Q0])});
            skLineSegment(sketch, "E72", {"start": v(0, 1.9) * mm, "end": v(-0.48, 1.9) * mm});
            skLineSegment(sketch, "E73", {"start": v(-0.48, 1.9) * mm, "end": v(-1.04, 2.58) * mm});
            skLineSegment(sketch, "E74", {"start": v(-1.04, 2.58) * mm, "end": v(-0.54, 2.46) * mm});
            skLineSegment(sketch, "E75", {"start": v(-0.54, 2.46) * mm, "end": v(-0.54, 2.2) * mm});
            skLineSegment(sketch, "E76", {"start": v(-0.23, 2.68) * mm, "end": v(0, 3.17) * mm});
            skFitSpline(sketch, "E77", {"points": [v(-1.08, 0.33) * mm, v(-0.46, 0.28) * mm, v(-0.22, 0.87) * mm, v(-0.44, 1.25) * mm, v(-1.56, 1.35) * mm, v(-2.04, -0.32) * mm, v(-0.35, -1.85) * mm], "startDerivative": vector(6.1, -3.56) * mm, "endDerivative": vector(8.59, -4.97) * mm});
            skFitSpline(sketch, "E78", {"points": [v(-0.35, -1.85) * mm, v(-1.11, -1.07) * mm, v(-1.7, 0) * mm, v(-1.3, 1.04) * mm, v(-0.7, 0.97) * mm, v(-1.08, 0.33) * mm], "startDerivative": vector(-3.34, 3.23) * mm, "endDerivative": vector(-10.41, 0.82) * mm});
            skFitSpline(sketch, "E79.MirrorCS", {"points": [v(1.08, 0.33) * mm, v(0.46, 0.28) * mm, v(0.22, 0.87) * mm, v(0.44, 1.25) * mm, v(1.56, 1.35) * mm, v(2.04, -0.32) * mm, v(0.35, -1.85) * mm], "startDerivative": vector(-6.1, -3.56) * mm, "endDerivative": vector(-8.59, -4.97) * mm});
            skFitSpline(sketch, "E80.MirrorCS", {"points": [v(0.35, -1.85) * mm, v(1.11, -1.07) * mm, v(1.7, 0) * mm, v(1.3, 1.04) * mm, v(0.7, 0.97) * mm, v(1.08, 0.33) * mm], "startDerivative": vector(3.34, 3.23) * mm, "endDerivative": vector(10.41, 0.82) * mm});
            skLineSegment(sketch, "E81.MirrorCS", {"start": v(0.23, 2.68) * mm, "end": v(0, 3.17) * mm});
            skLineSegment(sketch, "E82.MirrorCS", {"start": v(0.54, 2.46) * mm, "end": v(0.54, 2.2) * mm});
            skLineSegment(sketch, "E83.MirrorCS", {"start": v(1.04, 2.58) * mm, "end": v(0.54, 2.46) * mm});
            skLineSegment(sketch, "E84.MirrorCS", {"start": v(0.48, 1.9) * mm, "end": v(1.04, 2.58) * mm});
            skLineSegment(sketch, "E85.MirrorCS", {"start": v(0, 1.9) * mm, "end": v(0.48, 1.9) * mm});
            skFitSpline(sketch, "E86", {"points": [v(0.23, 2.68) * mm, v(0.16, 2.2) * mm, v(0.32, 2.05) * mm, v(0.54, 2.2) * mm], "startDerivative": vector(-0.38, -1.26) * mm, "endDerivative": vector(0.47, 1.27) * mm});
            skLineSegment(sketch, "E87", {"start": v(0, 0) * mm, "end": v(0, 1.7) * mm, "construction": true});
            skFitSpline(sketch, "E88.MirrorCS", {"points": [v(-0.23, 2.68) * mm, v(-0.16, 2.2) * mm, v(-0.32, 2.05) * mm, v(-0.54, 2.2) * mm], "startDerivative": vector(0.38, -1.26) * mm, "endDerivative": vector(-0.47, 1.27) * mm});
            skSolve(sketch);
        }
        {
            var Q0;
            Q0 = qSketchRegion(id + "F29", true);
            extrude(context, id + "F30", {"entities" : qUnion([Q0]), "operationType" : NewBodyOperationType.REMOVE, "oppositeDirection" : true, "depth" : 25 * mm});
        }
        {
            var Q0;
            Q0=qCreatedBy(id+"F23.planeOp",FACE);
            var sketch = newSketch(context, id + "F31", { "sketchPlane" : qUnion([Q0])});
            skLineSegment(sketch, "E89", {"start": v(0, 0) * mm, "end": v(0, 3.23) * mm, "construction": true});
            skLineSegment(sketch, "E90", {"start": v(0, 0.43) * mm, "end": v(2.38, 1.05) * mm});
            skLineSegment(sketch, "E91", {"start": v(2.38, 1.05) * mm, "end": v(0.37, -0.26) * mm});
            skLineSegment(sketch, "E92", {"start": v(0.37, -0.26) * mm, "end": v(0, -2.23) * mm});
            skLineSegment(sketch, "E93.MirrorCS", {"start": v(0, 0.43) * mm, "end": v(-2.38, 1.05) * mm});
            skLineSegment(sketch, "E94.MirrorCS", {"start": v(-2.38, 1.05) * mm, "end": v(-0.37, -0.26) * mm});
            skLineSegment(sketch, "E95.MirrorCS", {"start": v(-0.37, -0.26) * mm, "end": v(0, -2.23) * mm});
            skCircle(sketch, "E96", {"center": v(0, 0) * mm, "radius": 2.5 * mm, "construction": true});
            skLineSegment(sketch, "E97", {"start": v(2.14, 0.46) * mm, "end": v(2.46, 0.46) * mm});
            skSolve(sketch);
        }
        {
            var Q0;
            Q0 = qSketchRegion(id + "F31", true);
            extrude(context, id + "F32", {"entities" : qUnion([Q0]), "operationType" : NewBodyOperationType.REMOVE, "oppositeDirection" : true, "depth" : 25 * mm});
        }
        {
            var Q0;
            Q0=qCreatedBy(id+"F24.planeOp",FACE);
            var sketch = newSketch(context, id + "F33", { "sketchPlane" : qUnion([Q0])});
            skCircle(sketch, "E98", {"center": v(0, 0) * mm, "radius": 2.33 * mm, "construction": true});
            skArc(sketch, "E99", {"start": v(2.27, 0.52) * mm, "mid": v(0, 2.34) * mm, "end": v(-2.27, 0.52) * mm});
            skLineSegment(sketch, "E100", {"start": v(2.27, 0.52) * mm, "end": v(0.98, 0.52) * mm});
            skArc(sketch, "E101.MirrorCS", {"start": v(2.27, -0.52) * mm, "mid": v(0, -2.34) * mm, "end": v(-2.27, -0.52) * mm});
            skLineSegment(sketch, "E102", {"start": v(0, 0) * mm, "end": v(0, 1.54) * mm, "construction": true});
            skLineSegment(sketch, "E103.MirrorCS", {"start": v(-2.27, 0.52) * mm, "end": v(-0.98, 0.52) * mm});
            skLineSegment(sketch, "E104.MirrorCS", {"start": v(2.27, -0.52) * mm, "end": v(0.98, -0.52) * mm});
            skLineSegment(sketch, "E105.MirrorCS", {"start": v(-2.27, -0.52) * mm, "end": v(-0.98, -0.52) * mm});
            skArc(sketch, "E106", {"start": v(0.98, 0.52) * mm, "mid": v(0, 1.16) * mm, "end": v(-0.98, 0.52) * mm});
            skArc(sketch, "E107.MirrorCS", {"start": v(0.98, -0.52) * mm, "mid": v(0, -1.16) * mm, "end": v(-0.98, -0.52) * mm});
            skCircle(sketch, "E108", {"center": v(0, 0) * mm, "radius": 0.4 * mm});
            skSolve(sketch);
        }
        {
            var Q0;
            Q0 = qSketchRegion(id + "F33", true);
            extrude(context, id + "F34", {"entities" : qUnion([Q0]), "operationType" : NewBodyOperationType.REMOVE, "oppositeDirection" : true, "depth" : 25 * mm});
        }
        {
            var Q0;
            Q0=qCreatedBy(makeId("Right.planeOp"),FACE);
            var sketch = newSketch(context, id + "F35", { "sketchPlane" : qUnion([Q0])});
            skFitSpline(sketch, "E109", {"points": [v(0, 0.85) * mm, v(-0.31, 0.38) * mm, v(-0.83, 0.55) * mm, v(-0.9, 1.21) * mm, v(-0.49, 1.98) * mm], "startDerivative": vector(-1.01, -2.45) * mm, "endDerivative": vector(2.83, 2.22) * mm});
            skFitSpline(sketch, "E110", {"points": [v(-0.49, 1.98) * mm, v(-1.64, 1.3) * mm, v(-2, 0.43) * mm, v(-1.64, -0.2) * mm], "startDerivative": vector(-2.98, -0.36) * mm, "endDerivative": vector(2.1, -2.5) * mm});
            skFitSpline(sketch, "E111", {"points": [v(-1.64, -0.2) * mm, v(-1.52, 0.3) * mm, v(-1.25, 0.17) * mm, v(-1.16, -0.2) * mm], "startDerivative": vector(-1.43, 1.55) * mm, "endDerivative": vector(0.32, -1.1) * mm});
            skFitSpline(sketch, "E112", {"points": [v(-1.16, -0.2) * mm, v(-1.04, 0) * mm, v(-0.85, 0) * mm, v(-0.72, -0.37) * mm, v(-1.02, -0.65) * mm, v(-1.47, -0.73) * mm, v(-2.18, -0.2) * mm], "startDerivative": vector(0.48, 1.88) * mm, "endDerivative": vector(-0.84, 1.96) * mm});
            skFitSpline(sketch, "E113", {"points": [v(-2.18, -0.2) * mm, v(-2.87, -0.62) * mm], "startDerivative": vector(-0.52, -0.26) * mm, "endDerivative": vector(-0.52, -0.26) * mm});
            skFitSpline(sketch, "E114", {"points": [v(-2.87, -0.62) * mm, v(-2.13, -1.13) * mm], "startDerivative": vector(0.45, -0.42) * mm, "endDerivative": vector(0.49, -0.46) * mm});
            skFitSpline(sketch, "E115", {"points": [v(-2.13, -1.13) * mm, v(-1.4, -0.94) * mm, v(-1.03, -1.13) * mm, v(-1.04, -1.16) * mm, v(-1.63, -1.45) * mm], "startDerivative": vector(1.17, 1.35) * mm, "endDerivative": vector(-2.94, -0.64) * mm});
            skFitSpline(sketch, "E116", {"points": [v(-1.63, -1.45) * mm, v(-1.3, -1.92) * mm], "startDerivative": vector(0.56, -0.28) * mm, "endDerivative": vector(0.56, -0.28) * mm});
            skFitSpline(sketch, "E117", {"points": [v(-1.3, -1.92) * mm, v(-0.96, -1.64) * mm], "startDerivative": vector(0.24, 0.2) * mm, "endDerivative": vector(0.24, 0.2) * mm});
            skFitSpline(sketch, "E118", {"points": [v(-0.96, -1.64) * mm, v(-1.04, -2.21) * mm], "startDerivative": vector(-0.08, -0.31) * mm, "endDerivative": vector(-0.08, -0.31) * mm});
            skFitSpline(sketch, "E119", {"points": [v(-1.04, -2.21) * mm, v(-0.77, -2.4) * mm], "startDerivative": vector(0.33, -0.18) * mm, "endDerivative": vector(0.33, -0.18) * mm});
            skFitSpline(sketch, "E120", {"points": [v(-0.77, -2.4) * mm, v(-0.48, -1.79) * mm], "startDerivative": vector(0.1, 0.35) * mm, "endDerivative": vector(0.1, 0.35) * mm});
            skFitSpline(sketch, "E121", {"points": [v(-0.47, -1.79) * mm, v(-0.38, -2.45) * mm], "startDerivative": vector(0.1, -0.46) * mm, "endDerivative": vector(0.1, -0.46) * mm});
            skFitSpline(sketch, "E122", {"points": [v(-0.38, -2.45) * mm, v(-0.14, -2.45) * mm], "startDerivative": vector(0.25, 0) * mm, "endDerivative": vector(0.25, 0) * mm});
            skFitSpline(sketch, "E123", {"points": [v(-0.14, -2.45) * mm, v(0, -1.86) * mm], "startDerivative": vector(0.13, 0.38) * mm, "endDerivative": vector(0.13, 0.38) * mm});
            skLineSegment(sketch, "E124", {"start": v(0, 0) * mm, "end": v(0, 0.85) * mm, "construction": true});
            skFitSpline(sketch, "E125.MirrorCS", {"points": [v(0, 0.85) * mm, v(0.31, 0.38) * mm, v(0.83, 0.55) * mm, v(0.9, 1.21) * mm, v(0.49, 1.98) * mm], "startDerivative": vector(1.01, -2.45) * mm, "endDerivative": vector(-2.83, 2.22) * mm});
            skFitSpline(sketch, "E126.MirrorCS", {"points": [v(0.49, 1.98) * mm, v(1.64, 1.3) * mm, v(2, 0.43) * mm, v(1.64, -0.2) * mm], "startDerivative": vector(2.98, -0.36) * mm, "endDerivative": vector(-2.1, -2.5) * mm});
            skFitSpline(sketch, "E127.MirrorCS", {"points": [v(1.64, -0.2) * mm, v(1.52, 0.3) * mm, v(1.25, 0.17) * mm, v(1.16, -0.2) * mm], "startDerivative": vector(1.43, 1.55) * mm, "endDerivative": vector(-0.32, -1.1) * mm});
            skFitSpline(sketch, "E128.MirrorCS", {"points": [v(1.16, -0.2) * mm, v(1.04, 0) * mm, v(0.85, 0) * mm, v(0.72, -0.37) * mm, v(1.02, -0.65) * mm, v(1.47, -0.73) * mm, v(2.18, -0.2) * mm], "startDerivative": vector(-0.48, 1.88) * mm, "endDerivative": vector(0.84, 1.96) * mm});
            skFitSpline(sketch, "E129.MirrorCS", {"points": [v(2.87, -0.62) * mm, v(2.13, -1.13) * mm], "startDerivative": vector(-0.45, -0.42) * mm, "endDerivative": vector(-0.49, -0.46) * mm});
            skFitSpline(sketch, "E130.MirrorCS", {"points": [v(2.13, -1.13) * mm, v(1.4, -0.94) * mm, v(1.03, -1.13) * mm, v(1.04, -1.16) * mm, v(1.63, -1.45) * mm], "startDerivative": vector(-1.17, 1.35) * mm, "endDerivative": vector(2.94, -0.64) * mm});
            skFitSpline(sketch, "E131.MirrorCS", {"points": [v(2.18, -0.2) * mm, v(2.87, -0.62) * mm], "startDerivative": vector(0.52, -0.26) * mm, "endDerivative": vector(0.52, -0.26) * mm});
            skFitSpline(sketch, "E132.MirrorCS", {"points": [v(0.96, -1.64) * mm, v(1.04, -2.21) * mm], "startDerivative": vector(0.08, -0.31) * mm, "endDerivative": vector(0.08, -0.31) * mm});
            skFitSpline(sketch, "E133.MirrorCS", {"points": [v(1.3, -1.92) * mm, v(0.96, -1.64) * mm], "startDerivative": vector(-0.24, 0.2) * mm, "endDerivative": vector(-0.24, 0.2) * mm});
            skFitSpline(sketch, "E134.MirrorCS", {"points": [v(1.63, -1.45) * mm, v(1.3, -1.92) * mm], "startDerivative": vector(-0.56, -0.28) * mm, "endDerivative": vector(-0.56, -0.28) * mm});
            skFitSpline(sketch, "E135.MirrorCS", {"points": [v(1.04, -2.21) * mm, v(0.77, -2.4) * mm], "startDerivative": vector(-0.33, -0.18) * mm, "endDerivative": vector(-0.33, -0.18) * mm});
            skFitSpline(sketch, "E136.MirrorCS", {"points": [v(0.77, -2.4) * mm, v(0.48, -1.79) * mm], "startDerivative": vector(-0.1, 0.35) * mm, "endDerivative": vector(-0.1, 0.35) * mm});
            skFitSpline(sketch, "E137.MirrorCS", {"points": [v(0.47, -1.79) * mm, v(0.38, -2.45) * mm], "startDerivative": vector(-0.1, -0.46) * mm, "endDerivative": vector(-0.1, -0.46) * mm});
            skFitSpline(sketch, "E138.MirrorCS", {"points": [v(0.38, -2.45) * mm, v(0.14, -2.45) * mm], "startDerivative": vector(-0.25, 0) * mm, "endDerivative": vector(-0.25, 0) * mm});
            skLineSegment(sketch, "E139", {"start": v(-0.15, 0.52) * mm, "end": v(-0.15, -0.45) * mm});
            skLineSegment(sketch, "E140", {"start": v(0.17, 0.5) * mm, "end": v(0.17, -0.47) * mm});
            skFitSpline(sketch, "E141", {"points": [v(-0.15, -0.45) * mm, v(-0.15, -0.69) * mm, v(-0.37, -0.87) * mm], "startDerivative": vector(0.1, -0.53) * mm, "endDerivative": vector(-0.51, -0.32) * mm});
            skFitSpline(sketch, "E142", {"points": [v(-0.37, -0.87) * mm, v(-0.16, -1.05) * mm, v(0, -1.28) * mm], "startDerivative": vector(0.45, -0.32) * mm, "endDerivative": vector(0.28, -0.5) * mm});
            skFitSpline(sketch, "E143.MirrorCS", {"points": [v(0.15, -0.45) * mm, v(0.15, -0.69) * mm, v(0.37, -0.87) * mm], "startDerivative": vector(-0.1, -0.53) * mm, "endDerivative": vector(0.51, -0.32) * mm});
            skFitSpline(sketch, "E144.MirrorCS", {"points": [v(0.37, -0.87) * mm, v(0.16, -1.05) * mm, v(0, -1.28) * mm], "startDerivative": vector(-0.45, -0.32) * mm, "endDerivative": vector(-0.28, -0.5) * mm});
            skLineSegment(sketch, "E145", {"start": v(0, -1.86) * mm, "end": v(0.14, -2.45) * mm});
            skSolve(sketch);
        }
        {
            var Q0;
            Q0 = qSketchRegion(id + "F35", true);
            extrude(context, id + "F36", {"entities" : qUnion([Q0]), "operationType" : NewBodyOperationType.REMOVE, "depth" : 25 * mm});
        }
        {
            var Q0;
            Q0=qCreatedBy(id+"F21.planeOp",FACE);
            var sketch = newSketch(context, id + "F37", { "sketchPlane" : qUnion([Q0])});
            skCircle(sketch, "E146", {"center": v(0, -0.07) * mm, "radius": 2.33 * mm, "construction": true});
            skArc(sketch, "E147", {"start": v(2.27, 0.45) * mm, "mid": v(0, 2.27) * mm, "end": v(-2.27, 0.45) * mm});
            skLineSegment(sketch, "E148", {"start": v(2.27, 0.45) * mm, "end": v(0.98, 0.45) * mm});
            skArc(sketch, "E149.MirrorCS", {"start": v(2.27, -0.6) * mm, "mid": v(0, -2.4) * mm, "end": v(-2.27, -0.6) * mm});
            skLineSegment(sketch, "E150", {"start": v(0, -0.07) * mm, "end": v(0, 1.47) * mm, "construction": true});
            skLineSegment(sketch, "E151.MirrorCS", {"start": v(-2.27, 0.45) * mm, "end": v(-0.98, 0.45) * mm});
            skLineSegment(sketch, "E152.MirrorCS", {"start": v(2.27, -0.6) * mm, "end": v(0.98, -0.6) * mm});
            skLineSegment(sketch, "E153.MirrorCS", {"start": v(-2.27, -0.6) * mm, "end": v(-0.98, -0.6) * mm});
            skArc(sketch, "E154", {"start": v(0.98, 0.45) * mm, "mid": v(0, 1.09) * mm, "end": v(-0.98, 0.45) * mm});
            skArc(sketch, "E155.MirrorCS", {"start": v(0.98, -0.6) * mm, "mid": v(0, -1.23) * mm, "end": v(-0.98, -0.6) * mm});
            skCircle(sketch, "E156", {"center": v(0, -0.07) * mm, "radius": 0.4 * mm});
            skSolve(sketch);
        }
        {
            var Q0;
            Q0=makeQuery(id+"F34.boolean.opBoolean","COPY",FACE,{"derivedFrom":makeQuery(id+"F34.opExtrude","CAP_FACE",FACE,{"disambiguationData":[OSD([sQuery(id+"F33.wireOp",EDGE,"E99"),sQuery(id+"F33.wireOp",EDGE,"E100"),sQuery(id+"F33.wireOp",EDGE,"E103.MirrorCS"),sQuery(id+"F33.wireOp",EDGE,"E106")])],"isStart":true})});
            var Q1;
            Q1=makeQuery(id+"F34.boolean.opBoolean","COPY",FACE,{"derivedFrom":makeQuery(id+"F34.opExtrude","CAP_FACE",FACE,{"disambiguationData":[OSD([sQuery(id+"F33.wireOp",EDGE,"E101.MirrorCS"),sQuery(id+"F33.wireOp",EDGE,"E104.MirrorCS"),sQuery(id+"F33.wireOp",EDGE,"E105.MirrorCS"),sQuery(id+"F33.wireOp",EDGE,"E107.MirrorCS")])],"isStart":true})});
            var Q2;
            Q2=makeQuery(id+"F34.boolean.opBoolean","COPY",FACE,{"derivedFrom":makeQuery(id+"F34.opExtrude","CAP_FACE",FACE,{"disambiguationData":[OSD([sQuery(id+"F33.wireOp",EDGE,"E108")])],"isStart":true})});
            var Q3;
            Q3=sQuery(id+"F37.wireOp",EDGE,"E147");
            var Q4;
            Q4=sQuery(id+"F37.wireOp",EDGE,"E148");
            var Q5;
            Q5=sQuery(id+"F37.wireOp",EDGE,"E149.MirrorCS");
            var Q6;
            Q6=sQuery(id+"F37.wireOp",EDGE,"E151.MirrorCS");
            var Q7;
            Q7=sQuery(id+"F37.wireOp",EDGE,"E152.MirrorCS");
            var Q8;
            Q8=sQuery(id+"F37.wireOp",EDGE,"E153.MirrorCS");
            var Q9;
            Q9=sQuery(id+"F37.wireOp",EDGE,"E154");
            var Q10;
            Q10=sQuery(id+"F37.wireOp",EDGE,"E155.MirrorCS");
            var Q11;
            Q11=sQuery(id+"F37.wireOp",EDGE,"E156");
            extrude(context, id + "F38", {"entities" : qUnion([Q0, Q1, Q2]), "operationType" : NewBodyOperationType.REMOVE, "surfaceEntities" : qUnion([Q3, Q4, Q5, Q6, Q7, Q8, Q9, Q10, Q11]), "oppositeDirection" : true, "depth" : 2 * mm});
        }
        {
            var Q0;
            Q0=qCreatedBy(makeId("Right.planeOp"),FACE);
            var sketch = newSketch(context, id + "F39", { "sketchPlane" : qUnion([Q0])});
            skFitSpline(sketch, "E157", {"points": [v(0, -1.56) * mm, v(-1.32, -0.32) * mm, v(-1.39, 0.56) * mm, v(-0.78, 1.14) * mm, v(-0.22, 0.96) * mm, v(0, 0.38) * mm], "startDerivative": vector(-5.74, 4.33) * mm, "endDerivative": vector(0.73, -3.93) * mm});
            skFitSpline(sketch, "E158.MirrorCS", {"points": [v(0, -1.56) * mm, v(1.32, -0.32) * mm, v(1.39, 0.56) * mm, v(0.78, 1.14) * mm, v(0.22, 0.96) * mm, v(0, 0.38) * mm], "startDerivative": vector(5.74, 4.33) * mm, "endDerivative": vector(-0.73, -3.93) * mm});
            skSolve(sketch);
        }
        {
            var Q0;
            Q0=makeQuery(id+"F39.imprint","IMPRINT",FACE,{"disambiguationData":[TD([[makeQuery(id+"F39.imprint","IMPRINT",EDGE,{"derivedFrom":sQuery(id+"F39.wireOp",EDGE,"E157")}),-1.0]])]});
            extrude(context, id + "F40", {"entities" : qUnion([Q0]), "operationType" : NewBodyOperationType.REMOVE, "depth" : 25 * mm});
        }
        {
            var Q0;
            Q0=qCreatedBy(id+"F22.planeOp",FACE);
            var sketch = newSketch(context, id + "F41", { "sketchPlane" : qUnion([Q0])});
            skLineSegment(sketch, "E159", {"start": v(0, 0) * mm, "end": v(0, 3.02) * mm, "construction": true});
            skLineSegment(sketch, "E160", {"start": v(0, 0.43) * mm, "end": v(2.38, 1.05) * mm});
            skLineSegment(sketch, "E161", {"start": v(2.38, 1.05) * mm, "end": v(0.37, -0.26) * mm});
            skLineSegment(sketch, "E162", {"start": v(0.37, -0.26) * mm, "end": v(0, -2.23) * mm});
            skLineSegment(sketch, "E163.MirrorCS", {"start": v(0, 0.43) * mm, "end": v(-2.38, 1.05) * mm});
            skLineSegment(sketch, "E164.MirrorCS", {"start": v(-2.38, 1.05) * mm, "end": v(-0.37, -0.26) * mm});
            skLineSegment(sketch, "E165.MirrorCS", {"start": v(-0.37, -0.26) * mm, "end": v(0, -2.23) * mm});
            skCircle(sketch, "E166", {"center": v(0, 0) * mm, "radius": 2.5 * mm, "construction": true});
            skLineSegment(sketch, "E167", {"start": v(2.14, 0.46) * mm, "end": v(2.46, 0.46) * mm});
            skSolve(sketch);
        }
        {
            var Q0;
            Q0 = qSketchRegion(id + "F41", true);
            extrude(context, id + "F42", {"entities" : qUnion([Q0]), "operationType" : NewBodyOperationType.REMOVE, "depth" : 25 * mm});
        }
    });
